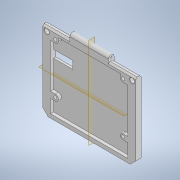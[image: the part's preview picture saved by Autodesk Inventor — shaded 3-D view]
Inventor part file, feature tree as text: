
AUTODESK INVENTOR PART (.ipt)
format: ipt  version: 2022 (Build 260153000, 153)  size: 227,328 bytes
history: native  units: mm
features: sketch x6, extrude x5, chamfer x3, other x3, plane x2, projected_geometry x2, reference x2, fillet x1, hole x1
ambient origin geometry x8: Origin, YZ Plane, XZ Plane, XY Plane, X Axis, Y Axis, Z Axis, Center Point
bodies: Solid1 (feature_tree)
feature tree (25):
  extrude  "Extrusion1"  Depth=7.0mm
  fillet  "Fillet1"  Radius=7.0mm
  extrude  "Extrusion2"  Depth=7.0mm TaperAngle=0.0deg
  plane  "Work Plane1"
  plane  "Work Plane2"
  chamfer  "Chamfer1"  [1 undecoded]
  extrude  "Extrusion3"  Depth=2.0mm TaperAngle=0.0deg
  chamfer  "Chamfer2"  Distance=2.0mm Angle=45.0deg
  extrude  "Extrusion4"  Depth=10.0mm
  hole  "Hole1"  [1 undecoded]
  extrude  "Extrusion5"  Depth=2.0mm
  chamfer  "Chamfer3"  Distance=4.0mm
  sketch  "Sketch1"  dims[d0=120.0mm d1=50.0mm d2=7.0mm]
  sketch  "Sketch2"  dims[d3=100.0mm d4=7.0mm d5=0.0mm]
  projected_geometry  "Projected Loop1"
  sketch  "Sketch3"  dims[d6=3.5mm]
  reference  "Reference1"
  reference  "Reference2"
  sketch  "Sketch4"  dims[d7=2.0mm d8=0.0mm d9=0.0mm]
  sketch  "Sketch5"  dims[d10=2.0mm d11=2.0mm d12=45.0deg d13=6.0mm d14=0.0mm d15=0.5mm d16=2.0mm d17=45.0deg]
  projected_geometry  "Projected Loop2"
  sketch  "Sketch6"  dims[d18=5.0mm d19=10.0mm d20=10.0mm d21=5.0mm d22=4.0mm d23=0.0mm d24=87.55mm d25=64.9mm d26=4.0mm d27=8.0mm d28=8.0mm d29=8.0mm d30=7.0mm d31=4.0mm d32=6.0mm d33=4.0mm d34=2.0mm d35=90.0deg d36=8.0mm d37=20.594885mm d38=0.0mm d39=0.0mm d40=20.0mm d41=10.0mm d42=25.0mm d43=7.0mm d44=2.0mm d45=45.0deg]
  parser-record x1  (decoder bookkeeping rows leaked as tree rows — omitted from the tree; the rows remain in map.json)
  other  "TFT35 Mount.iam"
  other  "LCD Mount 1:1"
note: 2 required parameter values undecoded (feature->parameter linkage not recoverable at this tier; creation-order binding heuristic only, values carry confidence <= 0.55)
note: 1 file-system path scrubbed to <path> (originals preserved in map.json)
